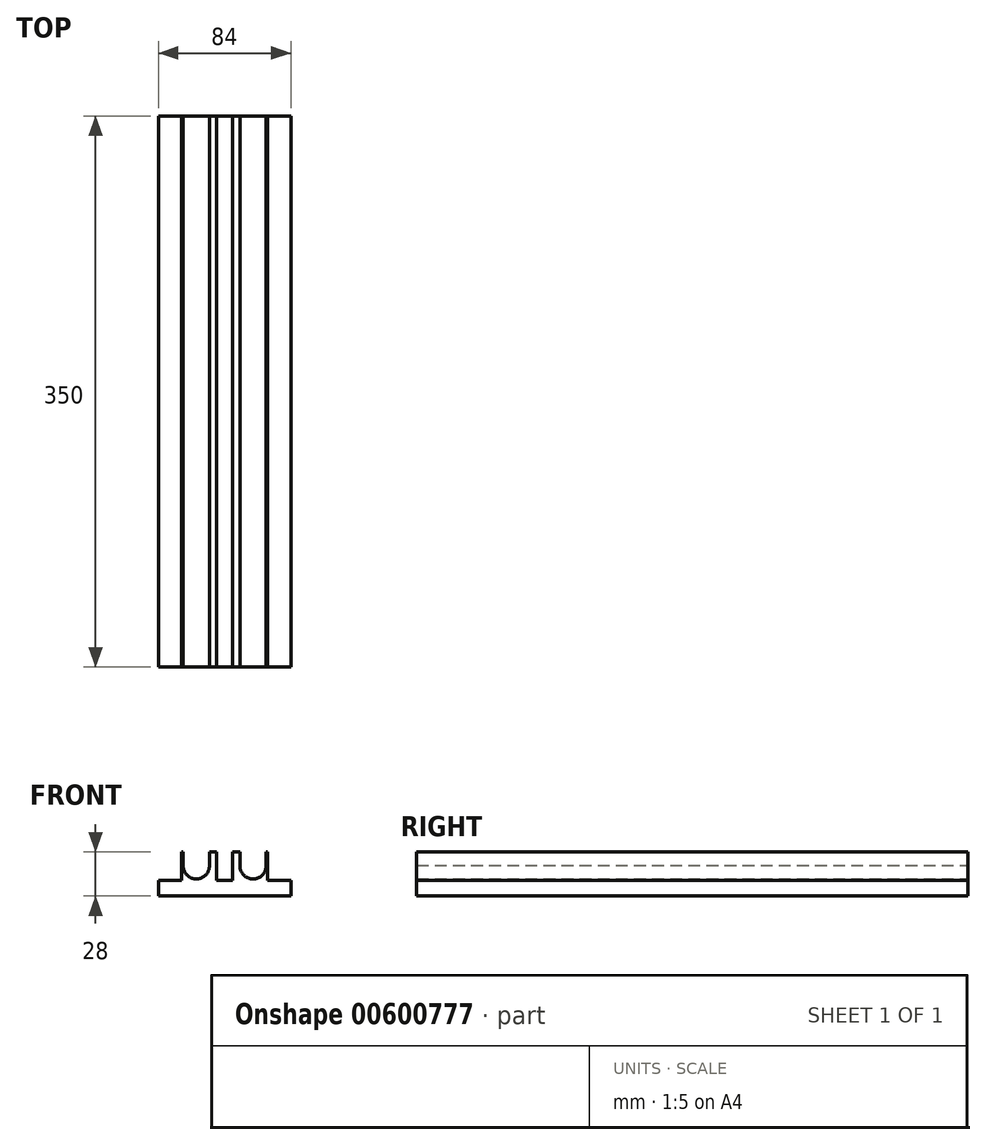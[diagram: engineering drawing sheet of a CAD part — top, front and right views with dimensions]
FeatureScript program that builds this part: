
annotation { "Feature Type Name" : "Feature", "Feature Type Description" : "" }
export const myFeature = defineFeature(function(context is Context, id is Id, definition is map)
    precondition{}
    {
        {
            var Q0;
            Q0=qCreatedBy(makeId("Front.planeOp"),FACE);
            var sketch = newSketch(context, id + "F0", { "sketchPlane" : qUnion([Q0])});
            skLineSegment(sketch, "E0.bottom", {"start": v(42, -14) * mm, "end": v(-42, -14) * mm});
            skLineSegment(sketch, "E0.top", {"start": v(27.35, 14) * mm, "end": v(26.35, 14) * mm});
            skLineSegment(sketch, "E0.left", {"start": v(42, -14) * mm, "end": v(42, -4) * mm});
            skLineSegment(sketch, "E0.right", {"start": v(-42, -14) * mm, "end": v(-42, -4) * mm});
            skPoint(sketch, "E0.middle", {"position": v(0, 0) * mm});
            skLineSegment(sketch, "E1", {"start": v(-42, -4) * mm, "end": v(-27.34, -4) * mm});
            skArc(sketch, "E2", {"start": v(-26.34, 5.45) * mm, "mid": v(-17.98, -3.2) * mm, "end": v(-9.66, 5.49) * mm});
            skArc(sketch, "E3", {"start": v(9.66, 5.45) * mm, "mid": v(17.99, -3.2) * mm, "end": v(26.35, 5.43) * mm});
            skLineSegment(sketch, "E4", {"start": v(-9.66, 4.81) * mm, "end": v(-9.66, 14) * mm});
            skLineSegment(sketch, "E5", {"start": v(9.66, 5.45) * mm, "end": v(9.66, 14) * mm});
            skLineSegment(sketch, "E6", {"start": v(26.35, 5.43) * mm, "end": v(26.35, 14) * mm});
            skLineSegment(sketch, "E7", {"start": v(-26.34, 5.45) * mm, "end": v(-26.34, 14) * mm});
            skLineSegment(sketch, "E8.bottom", {"start": v(5, -4) * mm, "end": v(-5, -4) * mm});
            skLineSegment(sketch, "E8.left", {"start": v(5, -4) * mm, "end": v(5, 14) * mm});
            skLineSegment(sketch, "E8.right", {"start": v(-5, -4) * mm, "end": v(-5, 14) * mm});
            skPoint(sketch, "E8.middle", {"position": v(0, 14) * mm});
            skLineSegment(sketch, "E9", {"start": v(-27.34, 14) * mm, "end": v(-27.34, -4) * mm});
            skLineSegment(sketch, "E10", {"start": v(27.35, 14) * mm, "end": v(27.35, -4) * mm});
            skPoint(sketch, "E8.top.start.orphan", {"position": v(5, 32) * mm});
            skPoint(sketch, "E11.orphan", {"position": v(-5, 32) * mm});
            skLineSegment(sketch, "E12.trimOffspring", {"start": v(-5, 14) * mm, "end": v(-9.66, 14) * mm});
            skLineSegment(sketch, "E13.trimOffspring", {"start": v(-26.34, 14) * mm, "end": v(-27.34, 14) * mm});
            skLineSegment(sketch, "E14.trimOffspring", {"start": v(9.66, 14) * mm, "end": v(5, 14) * mm});
            skLineSegment(sketch, "E15.trimOffspring", {"start": v(27.35, -4) * mm, "end": v(42, -4) * mm});
            skLineSegment(sketch, "E16.trimOffspring", {"start": v(-5, -4) * mm, "end": v(5, -4) * mm});
            skPoint(sketch, "E17.orphan", {"position": v(-42, 14) * mm});
            skPoint(sketch, "E18.orphan", {"position": v(42, 14) * mm});
            skSolve(sketch);
        }
        {
            var Q0;
            {var subQ0=sQuery(id+"F0.wireOp",EDGE,"E4");var subQ1=sQuery(id+"F0.wireOp",EDGE,"E2");var subQ2=makeQuery(id+"F0.imprint","INTERSECT",VERTEX,{"disambiguationData":[OD(0.0)],"derivedFrom":[subQ1,subQ0]});Q0=makeQuery(id+"F0.imprint","IMPRINT",FACE,{"disambiguationData":[TD([[makeQuery(id+"F0.imprint","IMPRINT",EDGE,{"disambiguationData":[TD([[subQ2,1.0]])],"derivedFrom":subQ1}),1.0]])]});}
            var Q1;
            Q1=makeQuery(id+"F0.imprint","IMPRINT",FACE,{"disambiguationData":[TD([[makeQuery(id+"F0.imprint","IMPRINT",EDGE,{"derivedFrom":sQuery(id+"F0.wireOp",EDGE,"E0.bottom")}),-1.0]])]});
            extrude(context, id + "F1", {"entities" : qUnion([Q0, Q1]), "depth" : 350 * mm, "offsetDistance" : 25 * mm});
        }
    });
